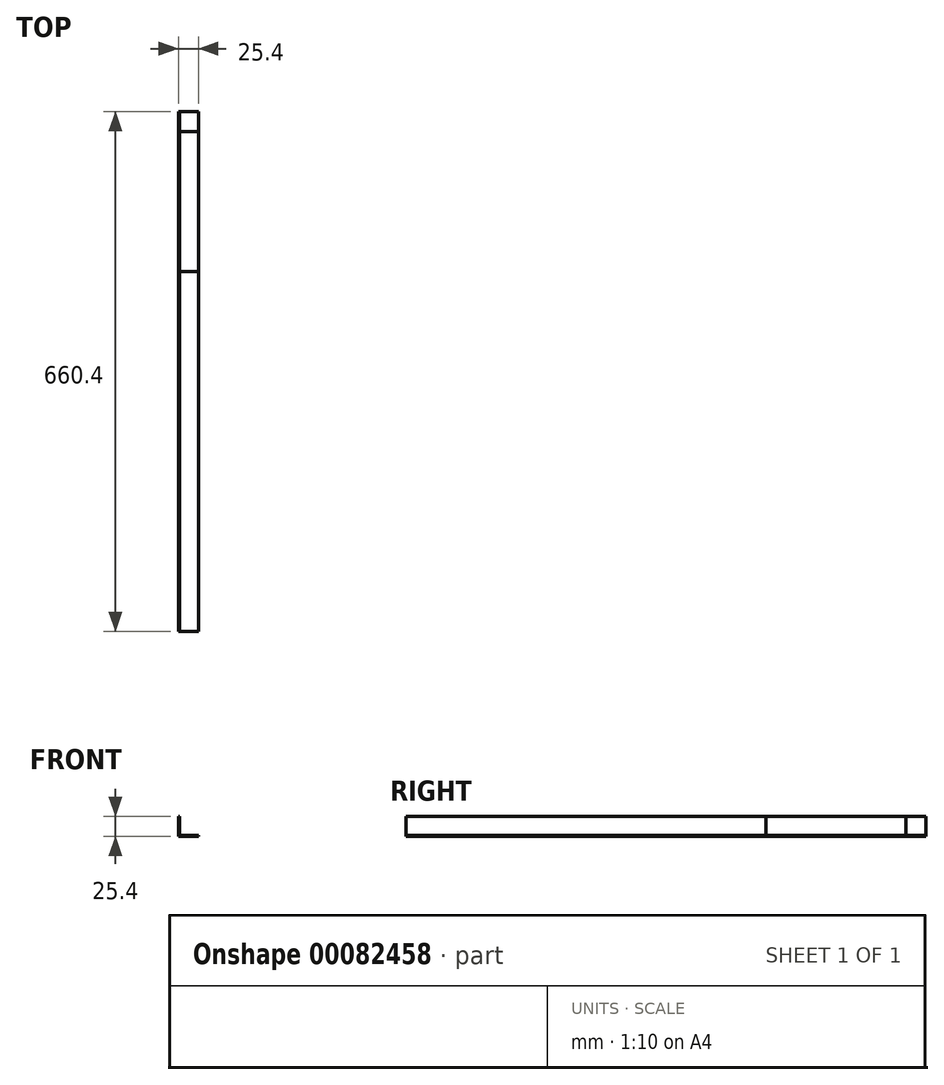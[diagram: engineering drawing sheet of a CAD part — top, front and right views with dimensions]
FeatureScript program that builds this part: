
annotation { "Feature Type Name" : "Feature", "Feature Type Description" : "" }
export const myFeature = defineFeature(function(context is Context, id is Id, definition is map)
    precondition{}
    {
        {
            var Q0;
            Q0=qCreatedBy(makeId("Front.planeOp"),FACE);
            var sketch = newSketch(context, id + "F0", { "sketchPlane" : qUnion([Q0])});
            skLineSegment(sketch, "E0", {"start": v(0, 0) * mm, "end": v(0, 25.4) * mm});
            skLineSegment(sketch, "E1", {"start": v(0, 25.4) * mm, "end": v(1.59, 25.4) * mm});
            skLineSegment(sketch, "E2", {"start": v(1.59, 25.4) * mm, "end": v(1.59, 1.59) * mm});
            skLineSegment(sketch, "E3", {"start": v(1.59, 1.59) * mm, "end": v(25.4, 1.59) * mm});
            skLineSegment(sketch, "E4", {"start": v(25.4, 1.59) * mm, "end": v(25.4, 0) * mm});
            skLineSegment(sketch, "E5", {"start": v(25.4, 0) * mm, "end": v(0, 0) * mm});
            skSolve(sketch);
        }
        {
            var Q0;
            Q0=makeQuery(id+"F0.imprint","IMPRINT",FACE,{"disambiguationData":[TD([[makeQuery(id+"F0.imprint","IMPRINT",EDGE,{"derivedFrom":sQuery(id+"F0.wireOp",EDGE,"E0")}),-1.0]])]});
            extrude(context, id + "F1", {"entities" : qUnion([Q0]), "depth" : 203.2 * mm});
        }
        {
            var Q0;
            Q0=qSketchRegion(id+"F0",true);
            extrude(context, id + "F2", {"entities" : qUnion([Q0]), "depth" : 660.4 * mm});
        }
        {
            var Q0;
            Q0 = qSketchRegion(id + "F0", true);
            extrude(context, id + "F3", {"entities" : qUnion([Q0]), "depth" : 25.4 * mm});
        }
    });
